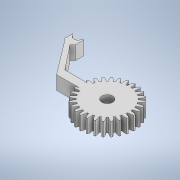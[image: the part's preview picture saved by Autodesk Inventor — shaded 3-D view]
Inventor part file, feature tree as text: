
AUTODESK INVENTOR PART (.ipt)
format: ipt  version: 2022 (Build 260153000, 153)  size: 337,408 bytes
history: native  units: in
note: dims shown in document units (in); Inventor stores cm internally (conversion verified against a paired STEP export)
features: extrude x7, sketch x7, pattern_circular x1
ambient origin geometry x8: Origin, YZ Plane, XZ Plane, XY Plane, X Axis, Y Axis, Z Axis, Center Point
bodies: Solid1 (feature_tree)
feature tree (15):
  extrude  "Extrusion1"  Depth=0.1575in
  pattern_circular  "Circular Pattern1"  [2 undecoded]
  extrude  "Extrusion2"  Depth=0.1181in TaperAngle=360.0deg
  extrude  "Extrusion3"  Depth=0.1181in
  extrude  "Extrusion4"  Depth=0.1181in
  extrude  "Extrusion5"  Depth=0.1181in
  extrude  "Extrusion6"  Depth=0.1575in
  extrude  "Extrusion7"  Depth=0.0787in
  sketch  "Sketch1"  dims[d0=0.6299in d1=0.1575in]
  sketch  "Sketch2"  dims[d2=0.0098in]
  sketch  "Sketch3"  dims[d3=0.0098in]
  sketch  "Sketch5"  dims[d4=0.0236in]
  sketch  "Sketch7"  dims[d7=0.0472in]
  sketch  "Sketch8"  dims[d8=0.1772in]
  sketch  "Sketch9"  dims[d10=0.0787in d11=0.1969in d12=0.0in d13=11.0236in d14=360.0deg d16=0.1181in d17=0.9843in d18=1.1322in d19=0.1575in d20=0.0787in d21=0.5512in d22=0.5512in d23=0.1969in d24=0.0in d25=0.1969in d26=0.1969in d27=0.0in d29=0.3937in d30=0.1181in d31=0.3563in d32=0.0in d43=0.9843in d44=1.1322in d45=0.0787in d46=0.1575in d47=0.1969in d48=0.0in d49=0.0394in d50=0.1181in d51=0.0394in d52=0.1181in d53=0.1969in d54=0.0in d55=0.1575in d56=0.1181in d57=0.0945in d58=0.0in d59=0.0in]
note: 2 required parameter values undecoded (feature->parameter linkage not recoverable at this tier; creation-order binding heuristic only, values carry confidence <= 0.55)
